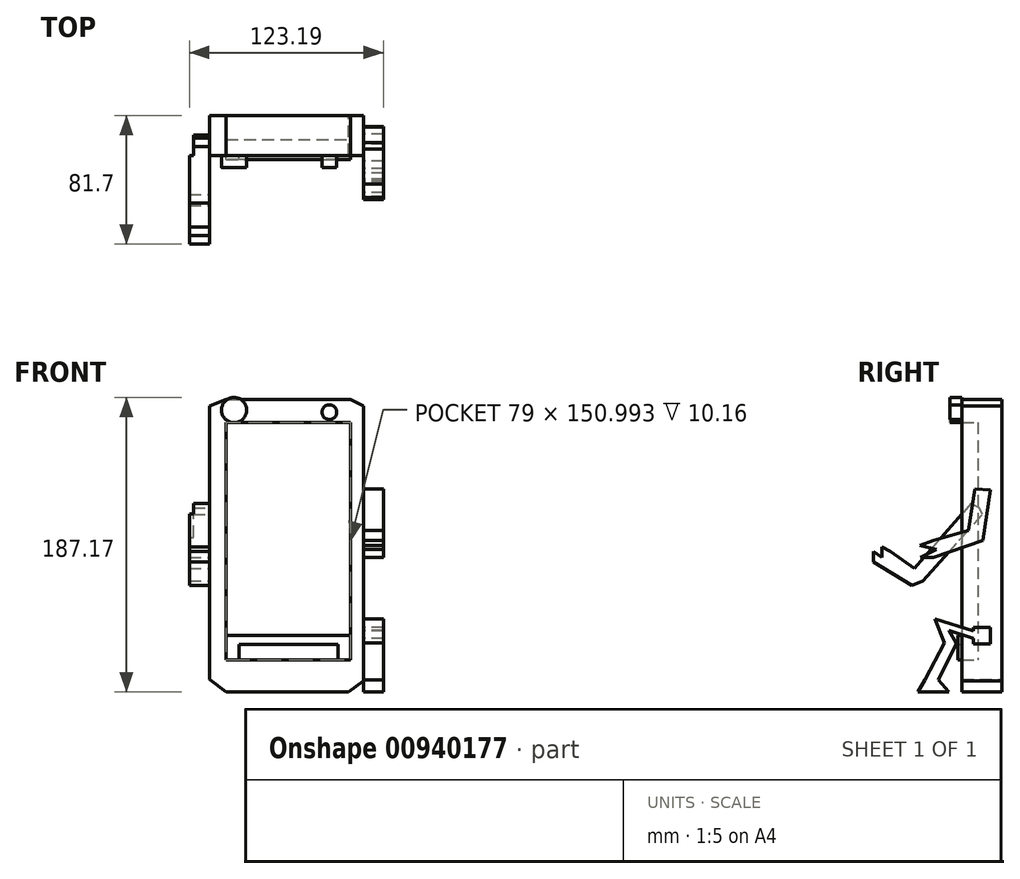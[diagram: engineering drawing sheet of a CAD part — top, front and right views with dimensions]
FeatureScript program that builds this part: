
annotation { "Feature Type Name" : "Feature", "Feature Type Description" : "" }
export const myFeature = defineFeature(function(context is Context, id is Id, definition is map)
    precondition{}
    {
        {
            var Q0;
            Q0=qCreatedBy(makeId("Front.planeOp"),FACE);
            var sketch = newSketch(context, id + "F0", { "sketchPlane" : qUnion([Q0])});
            skLineSegment(sketch, "E0", {"start": v(-76.67, 96.99) * mm, "end": v(-76.67, -54) * mm});
            skLineSegment(sketch, "E1", {"start": v(-76.67, -54) * mm, "end": v(-155.67, -54) * mm});
            skLineSegment(sketch, "E2", {"start": v(-155.67, -54) * mm, "end": v(-155.67, 96.99) * mm});
            skLineSegment(sketch, "E3", {"start": v(-155.67, 96.99) * mm, "end": v(-76.67, 96.99) * mm});
            skLineSegment(sketch, "E4", {"start": v(-155.67, -54) * mm, "end": v(-155.67, -74.24) * mm});
            skLineSegment(sketch, "E5", {"start": v(-155.67, -74.24) * mm, "end": v(-166.22, -66.37) * mm});
            skLineSegment(sketch, "E6", {"start": v(-166.22, -66.37) * mm, "end": v(-166.22, -54) * mm});
            skLineSegment(sketch, "E7", {"start": v(-166.22, -54) * mm, "end": v(-155.67, -54) * mm});
            skLineSegment(sketch, "E8", {"start": v(-166.22, -54) * mm, "end": v(-166.22, 96.99) * mm});
            skLineSegment(sketch, "E9", {"start": v(-166.22, 96.99) * mm, "end": v(-155.67, 96.99) * mm});
            skLineSegment(sketch, "E10", {"start": v(-155.67, 111.6) * mm, "end": v(-166.22, 107.48) * mm});
            skLineSegment(sketch, "E11", {"start": v(-166.22, 107.48) * mm, "end": v(-166.22, 96.99) * mm});
            skLineSegment(sketch, "E12", {"start": v(-155.67, 111.6) * mm, "end": v(-155.67, 96.99) * mm});
            skLineSegment(sketch, "E13", {"start": v(-155.67, 111.6) * mm, "end": v(-76.67, 111.6) * mm});
            skLineSegment(sketch, "E14", {"start": v(-76.67, 111.6) * mm, "end": v(-76.67, 96.99) * mm});
            skLineSegment(sketch, "E15", {"start": v(-68.43, 107.48) * mm, "end": v(-68.43, 96.99) * mm});
            skLineSegment(sketch, "E16", {"start": v(-68.43, 96.99) * mm, "end": v(-76.67, 96.99) * mm});
            skLineSegment(sketch, "E17", {"start": v(-68.43, 96.99) * mm, "end": v(-68.43, -54) * mm});
            skLineSegment(sketch, "E18", {"start": v(-68.43, -54) * mm, "end": v(-76.67, -54) * mm});
            skLineSegment(sketch, "E19", {"start": v(-76.67, 111.6) * mm, "end": v(-68.43, 107.48) * mm});
            skLineSegment(sketch, "E20", {"start": v(-155.67, -74.24) * mm, "end": v(-77.74, -74.24) * mm});
            skLineSegment(sketch, "E21", {"start": v(-77.74, -74.24) * mm, "end": v(-76.67, -54) * mm});
            skLineSegment(sketch, "E22", {"start": v(-68.43, -54) * mm, "end": v(-68.43, -67.12) * mm});
            skLineSegment(sketch, "E23", {"start": v(-68.43, -67.12) * mm, "end": v(-77.74, -74.24) * mm});
            skPoint(sketch, "E24", {"position": v(-116.7, -74.24) * mm});
            skSolve(sketch);
        }
        {
            var Q0;
            Q0=makeQuery(id+"F0.imprint","IMPRINT",FACE,{"disambiguationData":[TD([[makeQuery(id+"F0.imprint","IMPRINT",EDGE,{"derivedFrom":sQuery(id+"F0.wireOp",EDGE,"E0")}),-1.0]])]});
            extrude(context, id + "F1", {"entities" : qUnion([Q0]), "depth" : 15.24 * mm, "offsetDistance" : 25.4 * mm});
        }
        {
            var Q0;
            Q0 = qSketchRegion(id + "F0", true);
            extrude(context, id + "F2", {"entities" : qUnion([Q0]), "operationType" : NewBodyOperationType.ADD, "depth" : 25.4 * mm, "offsetDistance" : 25.4 * mm});
        }
        {
            var Q0;
            Q0=makeQuery(id+"F2.opExtrude","CAP_FACE",FACE,{"disambiguationData":[OSD([sQuery(id+"F0.wireOp",EDGE,"E0"),sQuery(id+"F0.wireOp",EDGE,"E1"),sQuery(id+"F0.wireOp",EDGE,"E2"),sQuery(id+"F0.wireOp",EDGE,"E3"),sQuery(id+"F0.wireOp",EDGE,"E5"),sQuery(id+"F0.wireOp",EDGE,"E6"),sQuery(id+"F0.wireOp",EDGE,"E8"),sQuery(id+"F0.wireOp",EDGE,"E10"),sQuery(id+"F0.wireOp",EDGE,"E11"),sQuery(id+"F0.wireOp",EDGE,"E13"),sQuery(id+"F0.wireOp",EDGE,"E15"),sQuery(id+"F0.wireOp",EDGE,"E17"),sQuery(id+"F0.wireOp",EDGE,"E19"),sQuery(id+"F0.wireOp",EDGE,"E20"),sQuery(id+"F0.wireOp",EDGE,"E22"),sQuery(id+"F0.wireOp",EDGE,"E23")])],"isStart":false});
            var sketch = newSketch(context, id + "F3", { "sketchPlane" : qUnion([Q0])});
            skLineSegment(sketch, "E25", {"start": v(-76.67, -38.35) * mm, "end": v(-76.67, -44.1) * mm});
            skLineSegment(sketch, "E26", {"start": v(-76.67, -44.1) * mm, "end": v(-155.67, -44.1) * mm});
            skLineSegment(sketch, "E27", {"start": v(-155.67, -44.1) * mm, "end": v(-155.67, -38.35) * mm});
            skLineSegment(sketch, "E28", {"start": v(-155.67, -38.35) * mm, "end": v(-76.67, -38.35) * mm});
            skLineSegment(sketch, "E29", {"start": v(-155.67, -44.1) * mm, "end": v(-155.67, -54) * mm});
            skLineSegment(sketch, "E30", {"start": v(-155.67, -54) * mm, "end": v(-147.34, -54) * mm});
            skLineSegment(sketch, "E31", {"start": v(-147.34, -54) * mm, "end": v(-147.34, -44.1) * mm});
            skLineSegment(sketch, "E32", {"start": v(-76.67, -44.1) * mm, "end": v(-76.67, -54) * mm});
            skLineSegment(sketch, "E33", {"start": v(-76.67, -54) * mm, "end": v(-81.3, -54) * mm});
            skLineSegment(sketch, "E34", {"start": v(-81.3, -54) * mm, "end": v(-84.53, -54) * mm});
            skLineSegment(sketch, "E35", {"start": v(-84.53, -54) * mm, "end": v(-84.53, -44.1) * mm});
            skSolve(sketch);
        }
        {
            var Q0;
            Q0 = qSketchRegion(id + "F3", true);
            extrude(context, id + "F4", {"entities" : qUnion([Q0]), "depth" : 2.54 * mm, "offsetDistance" : 25.4 * mm});
        }
        {
            var Q0;
            Q0=makeQuery(id+"F2.opExtrude","CAP_FACE",FACE,{"disambiguationData":[OSD([sQuery(id+"F0.wireOp",EDGE,"E0"),sQuery(id+"F0.wireOp",EDGE,"E1"),sQuery(id+"F0.wireOp",EDGE,"E2"),sQuery(id+"F0.wireOp",EDGE,"E3"),sQuery(id+"F0.wireOp",EDGE,"E5"),sQuery(id+"F0.wireOp",EDGE,"E6"),sQuery(id+"F0.wireOp",EDGE,"E8"),sQuery(id+"F0.wireOp",EDGE,"E10"),sQuery(id+"F0.wireOp",EDGE,"E11"),sQuery(id+"F0.wireOp",EDGE,"E13"),sQuery(id+"F0.wireOp",EDGE,"E15"),sQuery(id+"F0.wireOp",EDGE,"E17"),sQuery(id+"F0.wireOp",EDGE,"E19"),sQuery(id+"F0.wireOp",EDGE,"E20"),sQuery(id+"F0.wireOp",EDGE,"E22"),sQuery(id+"F0.wireOp",EDGE,"E23")])],"isStart":false});
            var sketch = newSketch(context, id + "F5", { "sketchPlane" : qUnion([Q0])});
            skCircle(sketch, "E36", {"center": v(-150.57, 104.8) * mm, "radius": 8 * mm});
            skCircle(sketch, "E37", {"center": v(-90.03, 103.46) * mm, "radius": 4.68 * mm});
            skLineSegment(sketch, "E38", {"start": v(-162.94, 63.13) * mm, "end": v(-198.37, 47.9) * mm});
            skLineSegment(sketch, "E39", {"start": v(-198.37, 47.9) * mm, "end": v(-198.37, 21.84) * mm});
            skLineSegment(sketch, "E40", {"start": v(-198.37, 21.84) * mm, "end": v(-190.1, 9.44) * mm});
            skLineSegment(sketch, "E41", {"start": v(-190.1, 9.44) * mm, "end": v(-184.14, 13.4) * mm});
            skLineSegment(sketch, "E42", {"start": v(-184.14, 13.4) * mm, "end": v(-191.63, 24.63) * mm});
            skLineSegment(sketch, "E43", {"start": v(-191.63, 24.63) * mm, "end": v(-191.63, 45.97) * mm});
            skLineSegment(sketch, "E44", {"start": v(-191.63, 45.97) * mm, "end": v(-163.25, 58.88) * mm});
            skLineSegment(sketch, "E45", {"start": v(-72.1, 59.47) * mm, "end": v(-54.37, 46.8) * mm});
            skLineSegment(sketch, "E46", {"start": v(-54.37, 46.8) * mm, "end": v(-43.78, 54.77) * mm});
            skLineSegment(sketch, "E47", {"start": v(-43.78, 54.77) * mm, "end": v(-43.78, 63.36) * mm});
            skLineSegment(sketch, "E48", {"start": v(-43.78, 63.36) * mm, "end": v(-55.23, 70.02) * mm});
            skLineSegment(sketch, "E49", {"start": v(-55.23, 70.02) * mm, "end": v(-58.48, 64.45) * mm});
            skLineSegment(sketch, "E50", {"start": v(-58.48, 64.45) * mm, "end": v(-49.07, 58.97) * mm});
            skLineSegment(sketch, "E51", {"start": v(-49.07, 58.97) * mm, "end": v(-49.07, 54.77) * mm});
            skLineSegment(sketch, "E52", {"start": v(-49.07, 54.77) * mm, "end": v(-55.23, 51) * mm});
            skLineSegment(sketch, "E53", {"start": v(-55.23, 51) * mm, "end": v(-68.43, 60.42) * mm});
            skSolve(sketch);
        }
        {
            var Q0;
            Q0 = qSketchRegion(id + "F5", true);
            extrude(context, id + "F6", {"entities" : qUnion([Q0]), "operationType" : NewBodyOperationType.ADD, "depth" : 7.62 * mm, "offsetDistance" : 25.4 * mm});
        }
        {
            var Q0;
            Q0=makeQuery(id+"F2.opExtrude","SWEPT_FACE",FACE,{"disambiguationData":[OSD([sQuery(id+"F0.wireOp",EDGE,"E6"),sQuery(id+"F0.wireOp",EDGE,"E8"),sQuery(id+"F0.wireOp",EDGE,"E11")])]});
            var sketch = newSketch(context, id + "F7", { "sketchPlane" : qUnion([Q0])});
            skLineSegment(sketch, "E54", {"start": v(50.2, -3.78) * mm, "end": v(12.55, 38.39) * mm});
            skLineSegment(sketch, "E55", {"start": v(12.55, 38.39) * mm, "end": v(14.4, 42.57) * mm});
            skLineSegment(sketch, "E56", {"start": v(14.4, 42.57) * mm, "end": v(19.7, 45.45) * mm});
            skLineSegment(sketch, "E57", {"start": v(19.7, 45.45) * mm, "end": v(55.56, 4.32) * mm});
            skLineSegment(sketch, "E58", {"start": v(55.56, 4.32) * mm, "end": v(70.84, 14.93) * mm});
            skLineSegment(sketch, "E59", {"start": v(70.84, 14.93) * mm, "end": v(76.27, 17.76) * mm});
            skLineSegment(sketch, "E60", {"start": v(76.27, 17.76) * mm, "end": v(76.27, 11.3) * mm});
            skLineSegment(sketch, "E61", {"start": v(76.27, 11.3) * mm, "end": v(81.7, 14.93) * mm});
            skLineSegment(sketch, "E62", {"start": v(81.7, 14.93) * mm, "end": v(81.7, 8.2) * mm});
            skLineSegment(sketch, "E63", {"start": v(81.7, 8.2) * mm, "end": v(57.3, -6.5) * mm});
            skLineSegment(sketch, "E64", {"start": v(57.3, -6.5) * mm, "end": v(50.2, -3.78) * mm});
            skSolve(sketch);
        }
        {
            var Q0;
            {var subQ0=sQuery(id+"F7.wireOp",EDGE,"mR3oeAdP-Re37-A2KI-5Cgk-udMPALbBkYmh");Q0=makeQuery(id+"F7.imprint","IMPRINT",FACE,{"disambiguationData":[TD([[makeQuery(id+"F7.imprint","IMPRINT",EDGE,{"derivedFrom":subQ0}),-1.0]])]});}
            var Q1;
            {var subQ0=sQuery(id+"F7.wireOp",EDGE,"E55");Q1=makeQuery(id+"F7.imprint","IMPRINT",FACE,{"disambiguationData":[TD([[makeQuery(id+"F7.imprint","IMPRINT",EDGE,{"derivedFrom":subQ0}),-1.0]])]});}
            extrude(context, id + "F8", {"entities" : qUnion([Q0, Q1]), "operationType" : NewBodyOperationType.ADD, "depth" : 10.16 * mm, "offsetDistance" : 25.4 * mm});
        }
        {
            var Q0;
            Q0=makeQuery(id+"F2.opExtrude","SWEPT_FACE",FACE,{"disambiguationData":[OSD([sQuery(id+"F0.wireOp",EDGE,"E15"),sQuery(id+"F0.wireOp",EDGE,"E17"),sQuery(id+"F0.wireOp",EDGE,"E22")])]});
            var sketch = newSketch(context, id + "F9", { "sketchPlane" : qUnion([Q0])});
            skLineSegment(sketch, "E65", {"start": v(-18.13, -33.24) * mm, "end": v(-18.13, -43.78) * mm});
            skLineSegment(sketch, "E66", {"start": v(-18.13, -43.78) * mm, "end": v(-7.25, -43.78) * mm});
            skLineSegment(sketch, "E67", {"start": v(-7.25, -43.78) * mm, "end": v(-7.25, -33.24) * mm});
            skLineSegment(sketch, "E68", {"start": v(-7.25, -33.24) * mm, "end": v(-18.13, -33.24) * mm});
            skLineSegment(sketch, "E69", {"start": v(-18.13, -35.35) * mm, "end": v(-18.13, -33.24) * mm});
            skLineSegment(sketch, "E70", {"start": v(0, -74.04) * mm, "end": v(3.6, -74.04) * mm});
            skLineSegment(sketch, "E71", {"start": v(-18.13, -35.35) * mm, "end": v(-42.7, -27.9) * mm});
            skLineSegment(sketch, "E72", {"start": v(-42.7, -27.9) * mm, "end": v(-36.69, -43.08) * mm});
            skLineSegment(sketch, "E73", {"start": v(-36.69, -43.08) * mm, "end": v(-48.96, -66.66) * mm});
            skLineSegment(sketch, "E74", {"start": v(-48.96, -66.66) * mm, "end": v(-53.4, -74.37) * mm});
            skLineSegment(sketch, "E75", {"start": v(-53.4, -74.37) * mm, "end": v(-33.69, -74.37) * mm});
            skLineSegment(sketch, "E76", {"start": v(-33.69, -74.37) * mm, "end": v(-40.46, -66.66) * mm});
            skLineSegment(sketch, "E77", {"start": v(-40.46, -66.66) * mm, "end": v(-28.91, -43.3) * mm});
            skLineSegment(sketch, "E78", {"start": v(-28.91, -43.3) * mm, "end": v(-33.69, -35.15) * mm});
            skLineSegment(sketch, "E79", {"start": v(-33.69, -35.15) * mm, "end": v(-18.13, -40.12) * mm});
            skSolve(sketch);
        }
        {
            var Q0;
            {var subQ0=sQuery(id+"F9.wireOp",EDGE,"E72");Q0=makeQuery(id+"F9.imprint","IMPRINT",FACE,{"disambiguationData":[TD([[makeQuery(id+"F9.imprint","IMPRINT",EDGE,{"derivedFrom":subQ0}),1.0]])]});}
            var Q1;
            {var subQ1=sQuery(id+"F9.wireOp",EDGE,"E65");var subQ3=sQuery(id+"F9.wireOp",EDGE,"E79");var subQ4=makeQuery(id+"F9.imprint","INTERSECT",VERTEX,{"derivedFrom":[subQ1,subQ3]});Q1=makeQuery(id+"F9.imprint","IMPRINT",FACE,{"disambiguationData":[TD([[makeQuery(id+"F9.imprint","IMPRINT",EDGE,{"disambiguationData":[TD([[subQ4,1.0]])],"derivedFrom":subQ1}),-1.0]])]});}
            var Q2;
            {var subQ0=sQuery(id+"F9.wireOp",EDGE,"E66");Q2=makeQuery(id+"F9.imprint","IMPRINT",FACE,{"disambiguationData":[TD([[makeQuery(id+"F9.imprint","IMPRINT",EDGE,{"derivedFrom":subQ0}),1.0]])]});}
            extrude(context, id + "F10", {"entities" : qUnion([Q0, Q1, Q2]), "operationType" : NewBodyOperationType.ADD, "depth" : 12.7 * mm, "offsetDistance" : 25 * mm});
        }
        {
            var Q0;
            {var subQ5=sQuery(id+"F7.wireOp",EDGE,"E58");Q0=makeQuery(id+"F7.imprint","IMPRINT",FACE,{"disambiguationData":[TD([[makeQuery(id+"F7.imprint","IMPRINT",EDGE,{"derivedFrom":subQ5}),-1.0]])]});}
            extrude(context, id + "F11", {"entities" : qUnion([Q0]), "operationType" : NewBodyOperationType.ADD, "depth" : 12.7 * mm, "offsetDistance" : 25 * mm});
        }
        {
            var Q0;
            {var subQ13=sQuery(id+"F9.wireOp",EDGE,"E66");Q0=makeQuery(id+"F9.imprint","IMPRINT",FACE,{"disambiguationData":[TD([[makeQuery(id+"F9.imprint","IMPRINT",EDGE,{"derivedFrom":subQ13}),-1.0]])]});}
            var sketch = newSketch(context, id + "F12", { "sketchPlane" : qUnion([Q0])});
            skLineSegment(sketch, "E80", {"start": v(-17.13, 54.67) * mm, "end": v(-21.49, 28.36) * mm});
            skLineSegment(sketch, "E81", {"start": v(-21.49, 28.36) * mm, "end": v(-43.71, 22.1) * mm});
            skLineSegment(sketch, "E82", {"start": v(-43.71, 22.1) * mm, "end": v(-52.22, 18.73) * mm});
            skLineSegment(sketch, "E83", {"start": v(-52.22, 18.73) * mm, "end": v(-41.55, 16.18) * mm});
            skLineSegment(sketch, "E84", {"start": v(-41.55, 16.18) * mm, "end": v(-51.7, 11.16) * mm});
            skLineSegment(sketch, "E85", {"start": v(-51.7, 11.16) * mm, "end": v(-43.71, 11.16) * mm});
            skLineSegment(sketch, "E86", {"start": v(-43.71, 11.16) * mm, "end": v(-12, 22.1) * mm});
            skLineSegment(sketch, "E87", {"start": v(-12, 22.1) * mm, "end": v(-7.42, 54.01) * mm});
            skLineSegment(sketch, "E88", {"start": v(-7.42, 54.01) * mm, "end": v(-17.13, 54.67) * mm});
            skSolve(sketch);
        }
        {
            var Q0;
            {var subQ0=sQuery(id+"F12.wireOp",EDGE,"E82");Q0=makeQuery(id+"F12.imprint","IMPRINT",FACE,{"disambiguationData":[TD([[makeQuery(id+"F12.imprint","IMPRINT",EDGE,{"derivedFrom":subQ0}),1.0]])]});}
            var Q1;
            {var subQ7=sQuery(id+"F12.wireOp",EDGE,"E80");Q1=makeQuery(id+"F12.imprint","IMPRINT",FACE,{"disambiguationData":[TD([[makeQuery(id+"F12.imprint","IMPRINT",EDGE,{"derivedFrom":subQ7}),1.0]])]});}
            extrude(context, id + "F13", {"entities" : qUnion([Q0, Q1]), "operationType" : NewBodyOperationType.ADD, "depth" : 12.7 * mm, "offsetDistance" : 25 * mm});
        }
        {
            var Q0;
            Q0=makeQuery(id+"F2.opExtrude","CAP_EDGE",EDGE,{"disambiguationData":[OSD([sQuery(id+"F0.wireOp",EDGE,"E1")])],"isStart":false});
            cPoint(context, id + "F14", {"entities" : qUnion([Q0]), "parameter" : 0.5});
        }
        {
            var Q0;
            Q0 = qCreatedBy(id + "F14" ,VERTEX);
            var Q1;
            Q1=qCreatedBy(makeId("Right.planeOp"),FACE);
            cPlane(context, id + "F15", {"entities" : qUnion([Q0, Q1]), "cplaneType" : CPlaneType.PLANE_POINT, "offset" : 25 * mm, "width" : 150 * mm, "height" : 150 * mm});
        }
    });
